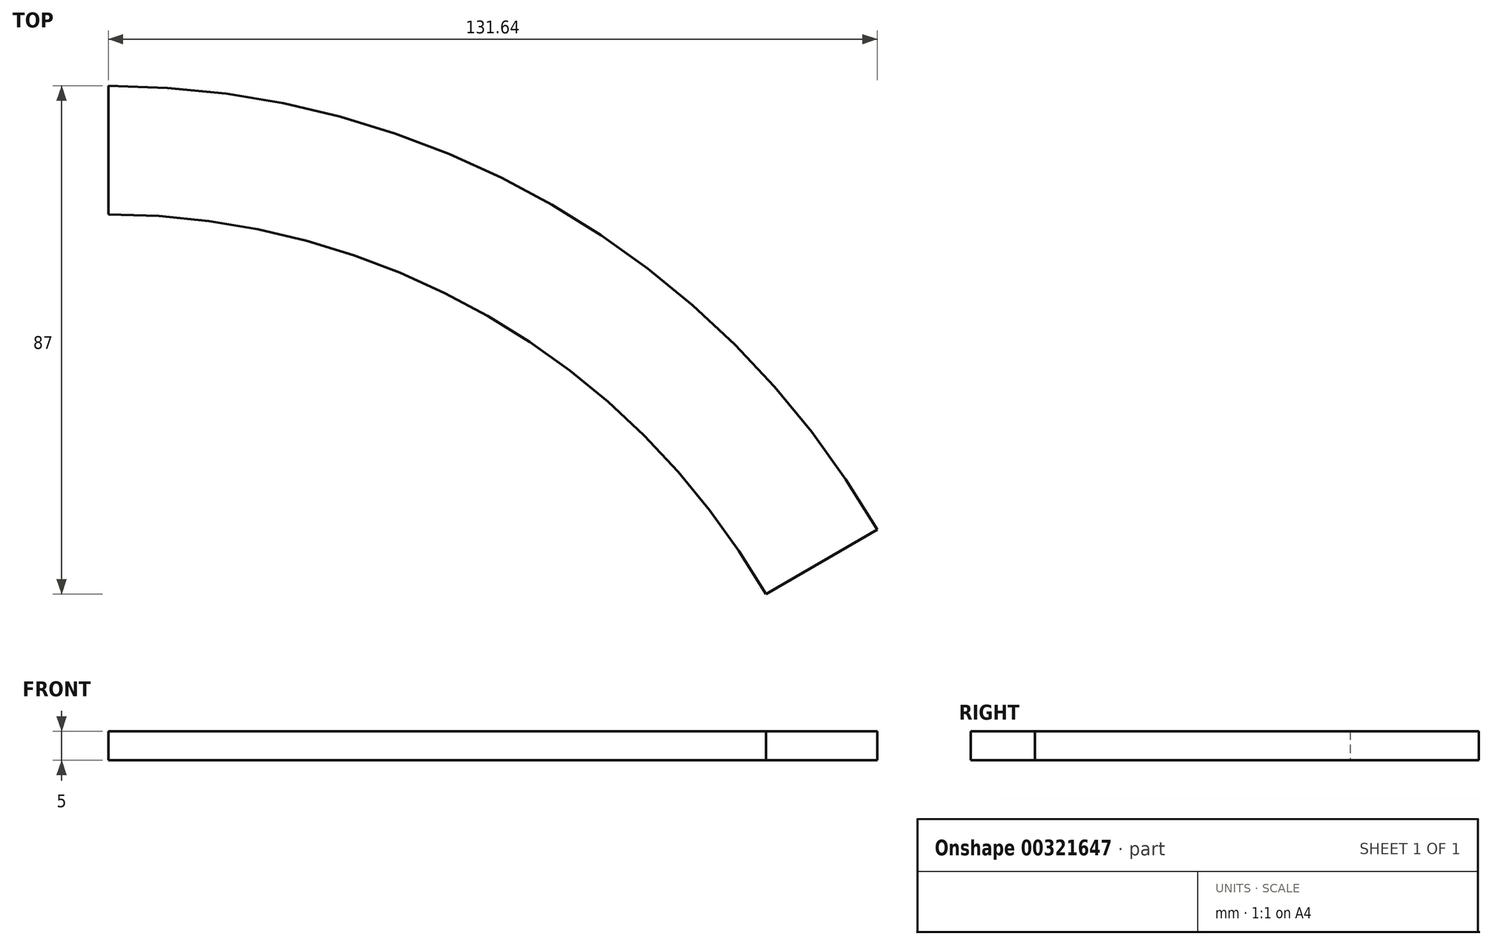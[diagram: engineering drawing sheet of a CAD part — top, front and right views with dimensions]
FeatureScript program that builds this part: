
annotation { "Feature Type Name" : "Feature", "Feature Type Description" : "" }
export const myFeature = defineFeature(function(context is Context, id is Id, definition is map)
    precondition{}
    {
        {
            var Q0;
            Q0=qCreatedBy(makeId("Top.planeOp"),FACE);
            var sketch = newSketch(context, id + "F0", { "sketchPlane" : qUnion([Q0])});
            skCircle(sketch, "E0", {"center": v(0, 0) * mm, "radius": 152 * mm});
            skCircle(sketch, "E1", {"center": v(0, 0) * mm, "radius": 130 * mm});
            skLineSegment(sketch, "E2", {"start": v(0, 0) * mm, "end": v(0, 152) * mm});
            skLineSegment(sketch, "E3.1.0", {"start": v(0, 0) * mm, "end": v(-131.64, 76) * mm});
            skLineSegment(sketch, "E3.2.0", {"start": v(0, 0) * mm, "end": v(-131.64, -76) * mm});
            skLineSegment(sketch, "E3.3.0", {"start": v(0, 0) * mm, "end": v(0, -152) * mm});
            skLineSegment(sketch, "E4.2.4.0", {"start": v(0, 0) * mm, "end": v(131.64, -76) * mm});
            skLineSegment(sketch, "E4.2.5.0", {"start": v(0, 0) * mm, "end": v(131.64, 76) * mm});
            skSolve(sketch);
        }
        {
            var Q0;
            {var subQ0=sQuery(id+"F0.wireOp",EDGE,"E2");var subQ1=sQuery(id+"F0.wireOp",EDGE,"E0");var subQ2=makeQuery(id+"F0.imprint","INTERSECT",VERTEX,{"derivedFrom":[subQ1,subQ0]});Q0=makeQuery(id+"F0.imprint","IMPRINT",FACE,{"disambiguationData":[TD([[makeQuery(id+"F0.imprint","IMPRINT",EDGE,{"disambiguationData":[TD([[subQ2,1.0]])],"derivedFrom":subQ1}),1.0]])]});}
            extrude(context, id + "F1", {"entities" : qUnion([Q0]), "depth" : 5 * mm});
        }
    });
